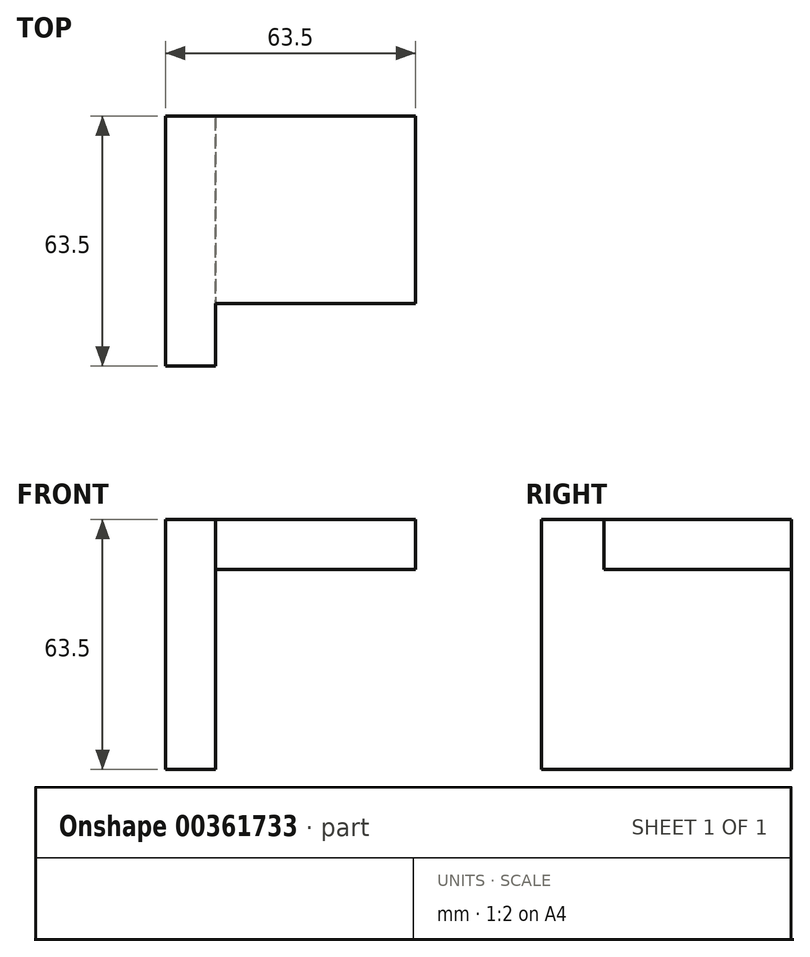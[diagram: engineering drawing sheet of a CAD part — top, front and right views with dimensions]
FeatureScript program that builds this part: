
annotation { "Feature Type Name" : "Feature", "Feature Type Description" : "" }
export const myFeature = defineFeature(function(context is Context, id is Id, definition is map)
    precondition{}
    {
        {
            var Q0;
            Q0=qCreatedBy(makeId("Front.planeOp"),FACE);
            var sketch = newSketch(context, id + "F0", { "sketchPlane" : qUnion([Q0])});
            skLineSegment(sketch, "E0.bottom", {"start": v(0, 0) * mm, "end": v(12.7, 0) * mm});
            skLineSegment(sketch, "E0.top", {"start": v(0, -63.5) * mm, "end": v(12.7, -63.5) * mm});
            skLineSegment(sketch, "E0.left", {"start": v(0, 0) * mm, "end": v(0, -63.5) * mm});
            skLineSegment(sketch, "E0.right", {"start": v(12.7, 0) * mm, "end": v(12.7, -63.5) * mm});
            skSolve(sketch);
        }
        {
            var Q0;
            Q0=makeQuery(id+"F0.imprint","IMPRINT",FACE,{"disambiguationData":[TD([[makeQuery(id+"F0.imprint","IMPRINT",EDGE,{"derivedFrom":sQuery(id+"F0.wireOp",EDGE,"E0.bottom")}),-1.0]])]});
            extrude(context, id + "F1", {"entities" : qUnion([Q0]), "depth" : 63.5 * mm});
        }
        {
            var Q0;
            Q0=qCreatedBy(makeId("Front.planeOp"),FACE);
            var sketch = newSketch(context, id + "F2", { "sketchPlane" : qUnion([Q0])});
            skLineSegment(sketch, "E1.bottom", {"start": v(0, 0) * mm, "end": v(63.5, 0) * mm});
            skLineSegment(sketch, "E1.top", {"start": v(0, -12.7) * mm, "end": v(63.5, -12.7) * mm});
            skLineSegment(sketch, "E1.left", {"start": v(0, 0) * mm, "end": v(0, -12.7) * mm});
            skLineSegment(sketch, "E1.right", {"start": v(63.5, 0) * mm, "end": v(63.5, -12.7) * mm});
            skSolve(sketch);
        }
        {
            var Q0;
            Q0 = qSketchRegion(id + "F0", true);
            var Q1;
            Q1=makeQuery(id+"F2.imprint","IMPRINT",FACE,{"disambiguationData":[TD([[makeQuery(id+"F2.imprint","IMPRINT",EDGE,{"derivedFrom":sQuery(id+"F2.wireOp",EDGE,"E1.bottom")}),-1.0]])]});
            var Q2;
            Q2=sQuery(id+"F2.wireOp",EDGE,"E1.bottom");
            var Q3;
            Q3=sQuery(id+"F2.wireOp",EDGE,"E1.top");
            extrude(context, id + "F3", {"entities" : qUnion([Q0, Q1]), "operationType" : NewBodyOperationType.ADD, "surfaceEntities" : qUnion([Q2, Q3]), "depth" : 47.62 * mm});
        }
    });
